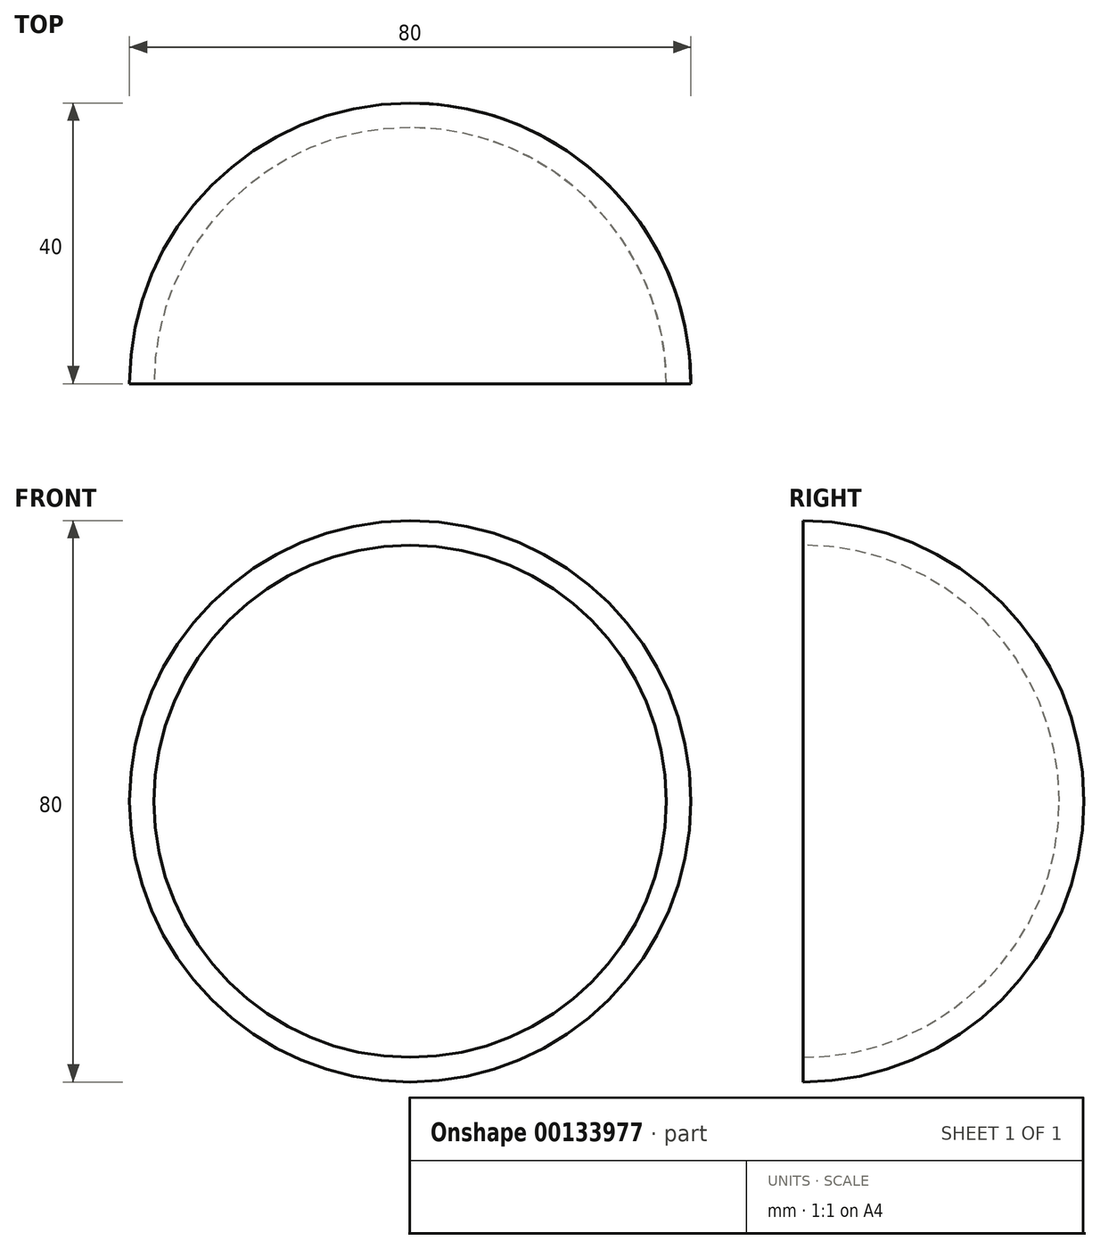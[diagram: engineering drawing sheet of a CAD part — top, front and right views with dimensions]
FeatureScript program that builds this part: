
annotation { "Feature Type Name" : "Feature", "Feature Type Description" : "" }
export const myFeature = defineFeature(function(context is Context, id is Id, definition is map)
    precondition{}
    {
        {
            var Q0;
            Q0=qCreatedBy(makeId("Top.planeOp"),FACE);
            var sketch = newSketch(context, id + "F0", { "sketchPlane" : qUnion([Q0])});
            skLineSegment(sketch, "E0", {"start": v(0, 56.6) * mm, "end": v(0, 36.5) * mm, "construction": true});
            skArc(sketch, "E1", {"start": v(40, 0) * mm, "mid": v(28.28, 28.28) * mm, "end": v(0, 40) * mm});
            skLineSegment(sketch, "E2", {"start": v(36.5, 0) * mm, "end": v(40, 0) * mm});
            skLineSegment(sketch, "E3", {"start": v(0, 0) * mm, "end": v(0, 40) * mm});
            skArc(sketch, "E4", {"start": v(36.5, 0) * mm, "mid": v(25.8, 25.8) * mm, "end": v(0, 36.5) * mm});
            skLineSegment(sketch, "E5.trimOffspring", {"start": v(0, 0) * mm, "end": v(0, -64.35) * mm, "construction": true});
            skSolve(sketch);
        }
        {
            var Q0;
            Q0=makeQuery(id+"F0.imprint","IMPRINT",FACE,{"disambiguationData":[TD([[makeQuery(id+"F0.imprint","IMPRINT",EDGE,{"derivedFrom":sQuery(id+"F0.wireOp",EDGE,"E1")}),1.0]])]});
            var Q1;
            Q1=sQuery(id+"F0.wireOp",EDGE,"E0");
            revolve(context, id + "F1", {"surfaceOperationType" : NewSurfaceOperationType.NEW, "entities" : qUnion([Q0]), "axis" : qUnion([Q1]), "revolveType" : RevolveType.FULL});
        }
    });
